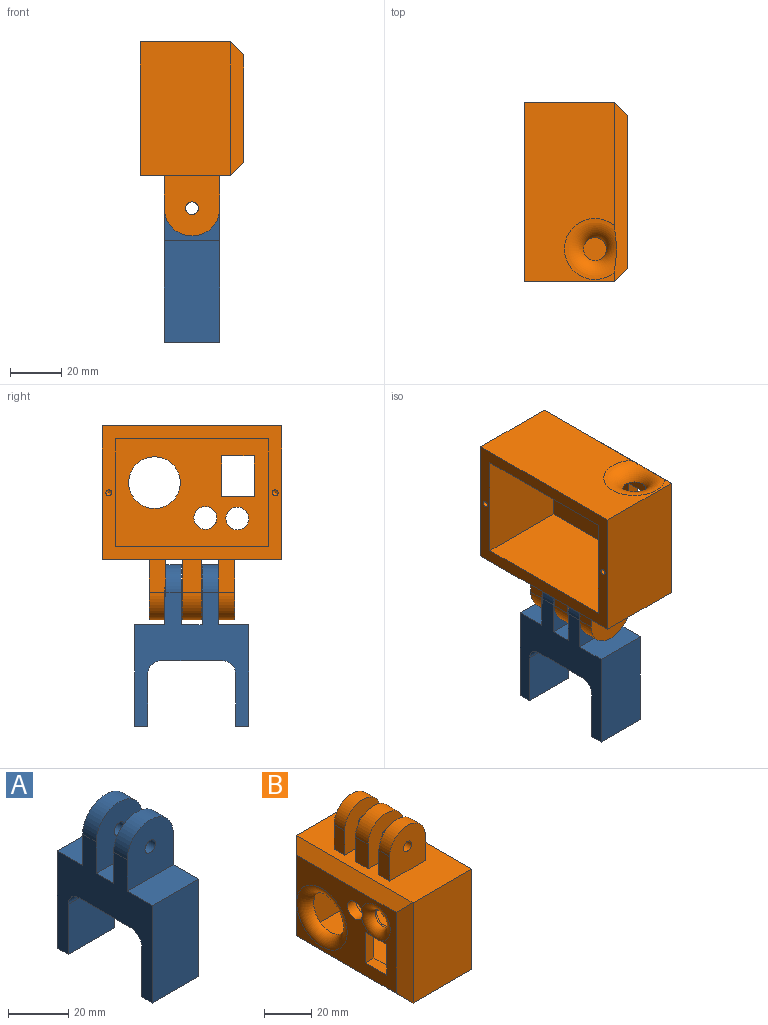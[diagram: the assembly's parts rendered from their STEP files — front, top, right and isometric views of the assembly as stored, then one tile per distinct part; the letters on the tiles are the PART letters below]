
ASSEMBLY  parts=2 mates=1
PART A: 22 faces, bbox 21.6x44.5x62.9 mm
  f0: plane 21.59x11.81mm, normal (0,0,1), area 255mm2, adj f3,f4,f7,f16
  f1: plane 21.59x8.13mm, normal (0,0,1), area 175.5mm2, adj f3,f4,f15,f17
  f2: plane 21.59x5.08mm, normal (0,0,-1), area 109.7mm2, adj f3,f4,f7,f9
  f3: plane 52.11x44.45mm, normal (-1,0,0), area 1051.8mm2, adj f0,f1,f2,f5,f6,f7,f8,f9
  f4: plane 52.11x44.45mm, normal (1,0,0), area 1051.8mm2, adj f0,f1,f2,f5,f6,f7,f8,f9
  f5: plane 21.59x5.08mm, normal (0,0,-1), area 109.7mm2, adj f3,f4,f6,f8
  f6: plane 39.41x21.59mm, normal (0,-1,0), area 850.8mm2, adj f3,f4,f5,f13
  f7: plane 39.41x21.59mm, normal (0,1,0), area 850.8mm2, adj f0,f2,f3,f4
  f8: plane 21.59x20.36mm, normal (0,1,0), area 439.5mm2, adj f3,f4,f5,f12
  f9: plane 21.59x20.36mm, normal (0,-1,0), area 439.5mm2, adj f2,f3,f4,f11
  f10: plane 24.13x21.59mm, normal (0,0,-1), area 521mm2, adj f3,f4,f11,f12
  f11: cylinder r=5.08mm len=21.59mm, axis (1,0,0), area 172.3mm2, adj f3,f4,f9,f10
  f12: cylinder r=5.08mm len=21.59mm, axis (-1,0,0), area 172.3mm2, adj f3,f4,f8,f10
  f13: plane 21.59x11.81mm, normal (0,0,1), area 255mm2, adj f3,f4,f6,f14
  f14: plane 23.5x21.59mm, normal (0,-1,0), area 438mm2, adj f3,f4,f13,f18,f21
  f15: plane 23.5x21.59mm, normal (0,1,0), area 438mm2, adj f1,f3,f4,f18,f21
  f16: plane 23.5x21.59mm, normal (0,1,0), area 438mm2, adj f0,f3,f4,f19,f20
  f17: plane 23.5x21.59mm, normal (0,-1,0), area 438mm2, adj f1,f3,f4,f19,f20
  f18: cylinder r=10.79mm len=21.59mm, axis (0,-1,0), area 215.4mm2, adj f3,f4,f14,f15
  f19: cylinder r=10.79mm len=21.59mm, axis (0,-1,0), area 215.4mm2, adj f3,f4,f16,f17
  f20: cylinder r=2.48mm len=6.35mm, axis (0,-1,0), area 98.8mm2, adj f16,f17
  f21: cylinder r=2.48mm len=6.35mm, axis (0,-1,0), area 98.8mm2, adj f14,f15
PART B: 48 faces, bbox 46.5x76.2x75.7 mm
  f0: plane 59.69x41.91mm, normal (-1,0,0), area 1281.5mm2, adj f26,f27,f28,f29,f31,f33,f34,f44
  f1: plane 59.69x41.91mm, normal (1,0,0), area 1858.4mm2, adj f22,f23,f24,f25,f26,f27,f28,f29
  f2: plane 69.85x52.07mm, normal (1,0,0), area 1127.3mm2, adj f3,f4,f5,f6,f22,f23,f24,f25
  f3: plane 69.85x35.05mm, normal (0,0,1), area 2009.7mm2, adj f2,f4,f6,f7,f8,f9,f10,f11
  f4: plane 52.07x35.05mm, normal (0,-1,0), area 1825.2mm2, adj f2,f3,f5,f44
  f5: plane 69.85x35.05mm, normal (0,0,-1), area 2059.3mm2, adj f2,f4,f6,f32,f47
  f6: plane 52.07x35.05mm, normal (0,1,0), area 1825.2mm2, adj f2,f3,f5,f45
  f7: plane 12.7x7.62mm, normal (-1,0,0), area 96.8mm2, adj f3,f9,f10,f20
  f8: plane 12.7x7.62mm, normal (1,0,0), area 96.8mm2, adj f3,f9,f10,f20
  f9: plane 23.5x21.59mm, normal (0,-1,0), area 438mm2, adj f3,f7,f8,f20,f43
  f10: plane 23.5x21.59mm, normal (0,1,0), area 438mm2, adj f3,f7,f8,f20,f43
  f11: plane 12.7x6.35mm, normal (1,0,0), area 80.6mm2, adj f3,f13,f14,f19
  f12: plane 12.7x6.35mm, normal (-1,0,0), area 80.6mm2, adj f3,f13,f14,f19
  f13: plane 23.5x21.59mm, normal (0,1,0), area 395.2mm2, adj f3,f11,f12,f19,f40
  f14: plane 23.5x21.59mm, normal (0,-1,0), area 438mm2, adj f3,f11,f12,f19,f42
  f15: plane 12.7x6.35mm, normal (1,0,0), area 80.6mm2, adj f3,f17,f18,f21
  f16: plane 12.7x6.35mm, normal (-1,0,0), area 80.6mm2, adj f3,f17,f18,f21
  f17: plane 23.5x21.59mm, normal (0,-1,0), area 438mm2, adj f3,f15,f16,f21,f39
  f18: plane 23.5x21.59mm, normal (0,1,0), area 438mm2, adj f3,f15,f16,f21,f39
  f19: cylinder r=10.79mm len=21.59mm, axis (0,1,0), area 215.4mm2, adj f11,f12,f13,f14
  f20: cylinder r=10.79mm len=21.59mm, axis (0,1,0), area 258.4mm2, adj f7,f8,f9,f10
  f21: cylinder r=10.79mm len=21.59mm, axis (0,1,0), area 215.4mm2, adj f15,f16,f17,f18
  f22: plane 59.69x35.05mm, normal (0,0,1), area 2030.2mm2, adj f1,f2,f23,f25,f32
  f23: plane 41.91x35.05mm, normal (0,-1,0), area 1469mm2, adj f1,f2,f22,f24
  f24: plane 59.69x35.05mm, normal (0,0,-1), area 2092.3mm2, adj f1,f2,f23,f25
  f25: plane 41.91x35.05mm, normal (0,1,0), area 1469mm2, adj f1,f2,f22,f24
  f26: plane 12.74x5.08mm, normal (0,0,1), area 64.7mm2, adj f0,f1,f27,f29
  f27: plane 15.86x5.08mm, normal (0,1,0), area 80.6mm2, adj f0,f1,f26,f28
  f28: plane 12.84x5.18mm, normal (0,0,-1), area 64.7mm2, adj f0,f1,f27,f29,f33
  f29: plane 15.86x5.08mm, normal (0,-1,0), area 80.6mm2, adj f0,f1,f26,f28
  f30: cylinder r=4.45mm len=8.89mm, axis (-1,0,0), area 22mm2, adj f1,f33
  f31: cylinder r=4.45mm len=8.89mm, axis (-1,0,0), area 141.9mm2, adj f0,f1,f33
  f32: torus R=11.87mm, axis (0,0,1), area 411.8mm2, adj f5,f22,f47
  f33: torus R=8.74mm, axis (1,0,0), area 252mm2, adj f0,f28,f30,f31
  f34: torus R=15.13mm, axis (1,0,0), area 596.2mm2, adj f0,f1
  f35: cone r=0mm half-angle=59deg, axis (1,0,0), area 4.8mm2, adj f36
  f36: cylinder r=1.14mm len=25.4mm, axis (1,0,0), area 182.4mm2, adj f2,f35
  f37: cone r=0mm half-angle=59deg, axis (1,0,0), area 4.8mm2, adj f38
  f38: cylinder r=1.14mm len=25.4mm, axis (1,0,0), area 182.4mm2, adj f2,f37
  f39: cylinder r=2.48mm len=6.35mm, axis (0,1,0), area 98.8mm2, adj f17,f18
  f40: cylinder r=4.45mm len=8.89mm, axis (0,1,0), area 70.9mm2, adj f13,f41
  f41: plane 8.89x8.89mm, normal (0,1,0), area 42.8mm2, adj f40,f42
  f42: cylinder r=2.48mm len=4.95mm, axis (0,1,0), area 59.3mm2, adj f14,f41
  f43: cylinder r=2.48mm len=7.62mm, axis (0,1,0), area 118.6mm2, adj f9,f10
  f44: plane 52.07x5.08mm, normal (-0.71,-0.71,0), area 337.6mm2, adj f0,f4,f46,f47
  f45: plane 52.07x5.08mm, normal (-0.71,0.71,0), area 337.6mm2, adj f0,f6,f46,f47
  f46: plane 69.85x5.08mm, normal (-0.71,0,0.71), area 465.3mm2, adj f0,f3,f44,f45
  f47: plane 69.85x5.08mm, normal (-0.71,0,-0.71), area 454.5mm2, adj f0,f5,f32,f44,f45
PLACE A at identity
PLACE B rot(axis=(0,1,0),180deg) t=(-10.02,-20.79,79.84)mm
MATE pin_slot B.f19 <-> A.f20  axis (0,1,0) through (-30.09,-32.64,67.4)mm
